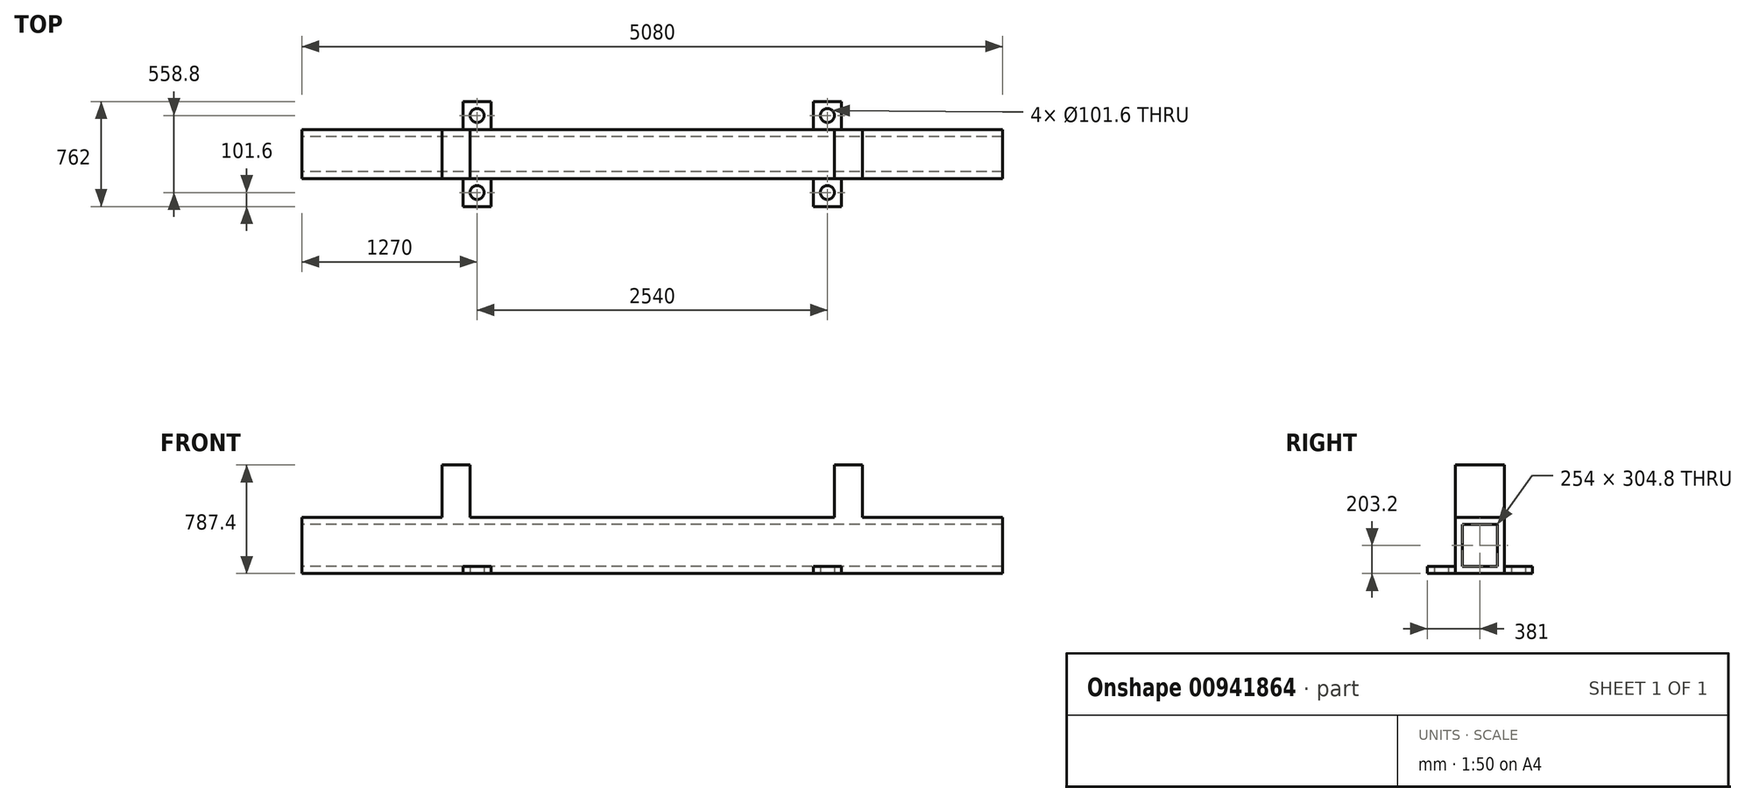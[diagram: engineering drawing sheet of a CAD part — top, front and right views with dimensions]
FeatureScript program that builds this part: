
annotation { "Feature Type Name" : "Feature", "Feature Type Description" : "" }
export const myFeature = defineFeature(function(context is Context, id is Id, definition is map)
    precondition{}
    {
        {
            var Q0;
            Q0=qCreatedBy(makeId("Top.planeOp"),FACE);
            var sketch = newSketch(context, id + "F0", { "sketchPlane" : qUnion([Q0])});
            skLineSegment(sketch, "E0.bottom", {"start": v(-2540, -177.8) * mm, "end": v(2540, -177.8) * mm});
            skLineSegment(sketch, "E0.top", {"start": v(-2540, 177.8) * mm, "end": v(2540, 177.8) * mm});
            skLineSegment(sketch, "E0.left", {"start": v(-2540, -177.8) * mm, "end": v(-2540, 177.8) * mm});
            skLineSegment(sketch, "E0.right", {"start": v(2540, -177.8) * mm, "end": v(2540, 177.8) * mm});
            skPoint(sketch, "E0.middle", {"position": v(0, 0) * mm});
            skLineSegment(sketch, "E1.bottom", {"start": v(-1371.6, -381) * mm, "end": v(-1168.4, -381) * mm});
            skLineSegment(sketch, "E1.top", {"start": v(-1371.6, 381) * mm, "end": v(-1168.4, 381) * mm});
            skLineSegment(sketch, "E1.left", {"start": v(-1371.6, -381) * mm, "end": v(-1371.6, 381) * mm});
            skLineSegment(sketch, "E1.right", {"start": v(-1168.4, -381) * mm, "end": v(-1168.4, 381) * mm});
            skPoint(sketch, "E1.middle", {"position": v(-1270, 0) * mm});
            skLineSegment(sketch, "E2.bottom", {"start": v(1168.4, -381) * mm, "end": v(1371.6, -381) * mm});
            skLineSegment(sketch, "E2.top", {"start": v(1168.4, 381) * mm, "end": v(1371.6, 381) * mm});
            skLineSegment(sketch, "E2.left", {"start": v(1168.4, -381) * mm, "end": v(1168.4, 381) * mm});
            skLineSegment(sketch, "E2.right", {"start": v(1371.6, -381) * mm, "end": v(1371.6, 381) * mm});
            skPoint(sketch, "E2.middle", {"position": v(1270, 0) * mm});
            skCircle(sketch, "E3", {"center": v(-1270, 279.4) * mm, "radius": 50.8 * mm});
            skCircle(sketch, "E4", {"center": v(-1270, -279.4) * mm, "radius": 50.8 * mm});
            skCircle(sketch, "E5", {"center": v(1270, 279.4) * mm, "radius": 50.8 * mm});
            skCircle(sketch, "E6", {"center": v(1270, -279.4) * mm, "radius": 50.8 * mm});
            skSolve(sketch);
        }
        {
            var Q0;
            {var subQ1=sQuery(id+"F0.wireOp",EDGE,"E1.top");Q0=makeQuery(id+"F0.imprint","IMPRINT",FACE,{"disambiguationData":[TD([[makeQuery(id+"F0.imprint","IMPRINT",EDGE,{"derivedFrom":subQ1}),-1.0]])]});}
            var Q1;
            {var subQ1=sQuery(id+"F0.wireOp",EDGE,"E1.bottom");Q1=makeQuery(id+"F0.imprint","IMPRINT",FACE,{"disambiguationData":[TD([[makeQuery(id+"F0.imprint","IMPRINT",EDGE,{"derivedFrom":subQ1}),1.0]])]});}
            var Q2;
            {var subQ0=sQuery(id+"F0.wireOp",EDGE,"E1.left");var subQ1=sQuery(id+"F0.wireOp",EDGE,"E0.bottom");var subQ2=makeQuery(id+"F0.imprint","INTERSECT",VERTEX,{"derivedFrom":[subQ1,subQ0]});Q2=makeQuery(id+"F0.imprint","IMPRINT",FACE,{"disambiguationData":[TD([[makeQuery(id+"F0.imprint","IMPRINT",EDGE,{"disambiguationData":[TD([[subQ2,-1.0]])],"derivedFrom":subQ1}),1.0]])]});}
            var Q3;
            {var subQ0=sQuery(id+"F0.wireOp",EDGE,"E1.right");var subQ1=sQuery(id+"F0.wireOp",EDGE,"E0.bottom");var subQ2=makeQuery(id+"F0.imprint","INTERSECT",VERTEX,{"derivedFrom":[subQ1,subQ0]});Q3=makeQuery(id+"F0.imprint","IMPRINT",FACE,{"disambiguationData":[TD([[makeQuery(id+"F0.imprint","IMPRINT",EDGE,{"disambiguationData":[TD([[subQ2,-1.0]])],"derivedFrom":subQ1}),1.0]])]});}
            var Q4;
            {var subQ0=sQuery(id+"F0.wireOp",EDGE,"E0.left");Q4=makeQuery(id+"F0.imprint","IMPRINT",FACE,{"disambiguationData":[TD([[makeQuery(id+"F0.imprint","IMPRINT",EDGE,{"derivedFrom":subQ0}),-1.0]])]});}
            var Q5;
            {var subQ0=sQuery(id+"F0.wireOp",EDGE,"E0.right");Q5=makeQuery(id+"F0.imprint","IMPRINT",FACE,{"disambiguationData":[TD([[makeQuery(id+"F0.imprint","IMPRINT",EDGE,{"derivedFrom":subQ0}),1.0]])]});}
            var Q6;
            {var subQ0=sQuery(id+"F0.wireOp",EDGE,"E2.left");var subQ1=sQuery(id+"F0.wireOp",EDGE,"E0.bottom");var subQ2=makeQuery(id+"F0.imprint","INTERSECT",VERTEX,{"derivedFrom":[subQ1,subQ0]});Q6=makeQuery(id+"F0.imprint","IMPRINT",FACE,{"disambiguationData":[TD([[makeQuery(id+"F0.imprint","IMPRINT",EDGE,{"disambiguationData":[TD([[subQ2,-1.0]])],"derivedFrom":subQ1}),1.0]])]});}
            var Q7;
            {var subQ1=sQuery(id+"F0.wireOp",EDGE,"E2.top");Q7=makeQuery(id+"F0.imprint","IMPRINT",FACE,{"disambiguationData":[TD([[makeQuery(id+"F0.imprint","IMPRINT",EDGE,{"derivedFrom":subQ1}),-1.0]])]});}
            var Q8;
            {var subQ1=sQuery(id+"F0.wireOp",EDGE,"E2.bottom");Q8=makeQuery(id+"F0.imprint","IMPRINT",FACE,{"disambiguationData":[TD([[makeQuery(id+"F0.imprint","IMPRINT",EDGE,{"derivedFrom":subQ1}),1.0]])]});}
            extrude(context, id + "F1", {"entities" : qUnion([Q0, Q1, Q2, Q3, Q4, Q5, Q6, Q7, Q8]), "depth" : 50.8 * mm, "offsetDistance" : 25.4 * mm});
        }
        {
            var Q0;
            {var subQ0=sQuery(id+"F0.wireOp",EDGE,"E1.right");var subQ1=sQuery(id+"F0.wireOp",EDGE,"E0.bottom");var subQ2=makeQuery(id+"F0.imprint","INTERSECT",VERTEX,{"derivedFrom":[subQ1,subQ0]});Q0=makeQuery(id+"F0.imprint","IMPRINT",FACE,{"disambiguationData":[TD([[makeQuery(id+"F0.imprint","IMPRINT",EDGE,{"disambiguationData":[TD([[subQ2,-1.0]])],"derivedFrom":subQ1}),1.0]])]});}
            var Q1;
            {var subQ0=sQuery(id+"F0.wireOp",EDGE,"E0.right");Q1=makeQuery(id+"F0.imprint","IMPRINT",FACE,{"disambiguationData":[TD([[makeQuery(id+"F0.imprint","IMPRINT",EDGE,{"derivedFrom":subQ0}),1.0]])]});}
            var Q2;
            {var subQ0=sQuery(id+"F0.wireOp",EDGE,"E0.left");Q2=makeQuery(id+"F0.imprint","IMPRINT",FACE,{"disambiguationData":[TD([[makeQuery(id+"F0.imprint","IMPRINT",EDGE,{"derivedFrom":subQ0}),-1.0]])]});}
            var Q3;
            {var subQ0=sQuery(id+"F0.wireOp",EDGE,"E1.left");var subQ1=sQuery(id+"F0.wireOp",EDGE,"E0.bottom");var subQ2=makeQuery(id+"F0.imprint","INTERSECT",VERTEX,{"derivedFrom":[subQ1,subQ0]});Q3=makeQuery(id+"F0.imprint","IMPRINT",FACE,{"disambiguationData":[TD([[makeQuery(id+"F0.imprint","IMPRINT",EDGE,{"disambiguationData":[TD([[subQ2,-1.0]])],"derivedFrom":subQ1}),1.0]])]});}
            var Q4;
            {var subQ0=sQuery(id+"F0.wireOp",EDGE,"E2.left");var subQ1=sQuery(id+"F0.wireOp",EDGE,"E0.bottom");var subQ2=makeQuery(id+"F0.imprint","INTERSECT",VERTEX,{"derivedFrom":[subQ1,subQ0]});Q4=makeQuery(id+"F0.imprint","IMPRINT",FACE,{"disambiguationData":[TD([[makeQuery(id+"F0.imprint","IMPRINT",EDGE,{"disambiguationData":[TD([[subQ2,-1.0]])],"derivedFrom":subQ1}),1.0]])]});}
            extrude(context, id + "F2", {"entities" : qUnion([Q0, Q1, Q2, Q3, Q4]), "operationType" : NewBodyOperationType.ADD, "depth" : 406.4 * mm, "offsetDistance" : 25.4 * mm});
        }
        {
            var Q0;
            {var subQ0=sQuery(id+"F0.wireOp",EDGE,"E0.left");Q0=makeQuery(id+"F2.boolean.opBoolean","MERGE",FACE,{"derivedFrom":[makeQuery(id+"F1.opExtrude","SWEPT_FACE",FACE,{"disambiguationData":[OSD([subQ0])]}),makeQuery(id+"F2.opExtrude","SWEPT_FACE",FACE,{"disambiguationData":[OSD([subQ0])]})]});}
            var sketch = newSketch(context, id + "F3", { "sketchPlane" : qUnion([Q0])});
            skLineSegment(sketch, "E7.bottom", {"start": v(-127, 50.8) * mm, "end": v(127, 50.8) * mm});
            skLineSegment(sketch, "E7.top", {"start": v(-127, 355.6) * mm, "end": v(127, 355.6) * mm});
            skLineSegment(sketch, "E7.left", {"start": v(-127, 50.8) * mm, "end": v(-127, 355.6) * mm});
            skLineSegment(sketch, "E7.right", {"start": v(127, 50.8) * mm, "end": v(127, 355.6) * mm});
            skPoint(sketch, "E7.middle", {"position": v(0, 203.2) * mm});
            skLineSegment(sketch, "E8.bottom", {"start": v(127, 355.6) * mm, "end": v(228.6, 355.6) * mm});
            skLineSegment(sketch, "E8.top", {"start": v(127, 203.2) * mm, "end": v(228.6, 203.2) * mm});
            skLineSegment(sketch, "E8.left", {"start": v(127, 355.6) * mm, "end": v(127, 203.2) * mm});
            skLineSegment(sketch, "E8.right", {"start": v(228.6, 355.6) * mm, "end": v(228.6, 203.2) * mm});
            skSolve(sketch);
        }
        {
            var Q0;
            Q0=makeQuery(id+"F3.imprint","IMPRINT",FACE,{"disambiguationData":[TD([[makeQuery(id+"F3.imprint","IMPRINT",EDGE,{"derivedFrom":sQuery(id+"F3.wireOp",EDGE,"E7.bottom")}),1.0]])]});
            var Q1;
            {var subQ0=sQuery(id+"F3.wireOp",EDGE,"E8.right");Q1=makeQuery(id+"F3.imprint","IMPRINT",FACE,{"disambiguationData":[TD([[makeQuery(id+"F3.imprint","IMPRINT",EDGE,{"derivedFrom":subQ0}),-1.0]])]});}
            var Q2;
            {var subQ0=sQuery(id+"F3.wireOp",EDGE,"E8.left");Q2=makeQuery(id+"F3.imprint","IMPRINT",FACE,{"disambiguationData":[TD([[makeQuery(id+"F3.imprint","IMPRINT",EDGE,{"derivedFrom":subQ0}),1.0]])]});}
            extrude(context, id + "F4", {"entities" : qUnion([Q0, Q1, Q2]), "operationType" : NewBodyOperationType.REMOVE, "oppositeDirection" : true, "depth" : 5963.92 * mm, "offsetDistance" : 25.4 * mm});
        }
        {
            var Q0;
            Q0=makeQuery(id+"F2.opExtrude","CAP_FACE",FACE,{"disambiguationData":[OSD([sQuery(id+"F0.wireOp",EDGE,"E0.bottom"),sQuery(id+"F0.wireOp",EDGE,"E0.top"),sQuery(id+"F0.wireOp",EDGE,"E0.left"),sQuery(id+"F0.wireOp",EDGE,"E0.right")])],"isStart":false});
            var sketch = newSketch(context, id + "F5", { "sketchPlane" : qUnion([Q0])});
            skPoint(sketch, "E9.middle", {"position": v(-1422.4, 0) * mm});
            skLineSegment(sketch, "E10", {"start": v(0, 0) * mm, "end": v(-2540, 0) * mm});
            skLineSegment(sketch, "E11", {"start": v(0, 0) * mm, "end": v(2540, 0) * mm});
            skPoint(sketch, "E12", {"position": v(1422.4, 0) * mm});
            skLineSegment(sketch, "E13.bottom", {"start": v(1320.8, -177.8) * mm, "end": v(1524, -177.8) * mm});
            skLineSegment(sketch, "E13.top", {"start": v(1320.8, 177.8) * mm, "end": v(1524, 177.8) * mm});
            skLineSegment(sketch, "E13.left", {"start": v(1320.8, -177.8) * mm, "end": v(1320.8, 177.8) * mm});
            skLineSegment(sketch, "E13.right", {"start": v(1524, -177.8) * mm, "end": v(1524, 177.8) * mm});
            skLineSegment(sketch, "E14.bottom", {"start": v(-1320.8, 177.8) * mm, "end": v(-1524, 177.8) * mm});
            skLineSegment(sketch, "E14.top", {"start": v(-1320.8, -177.8) * mm, "end": v(-1524, -177.8) * mm});
            skLineSegment(sketch, "E14.left", {"start": v(-1320.8, 177.8) * mm, "end": v(-1320.8, -177.8) * mm});
            skLineSegment(sketch, "E14.right", {"start": v(-1524, 177.8) * mm, "end": v(-1524, -177.8) * mm});
            skSolve(sketch);
        }
        {
            var Q0;
            {var subQ5=sQuery(id+"F5.wireOp",EDGE,"E13.top");Q0=makeQuery(id+"F5.imprint","IMPRINT",FACE,{"disambiguationData":[TD([[makeQuery(id+"F5.imprint","IMPRINT",EDGE,{"derivedFrom":subQ5}),-1.0]])]});}
            var Q1;
            {var subQ5=sQuery(id+"F5.wireOp",EDGE,"E13.bottom");Q1=makeQuery(id+"F5.imprint","IMPRINT",FACE,{"disambiguationData":[TD([[makeQuery(id+"F5.imprint","IMPRINT",EDGE,{"derivedFrom":subQ5}),1.0]])]});}
            var Q2;
            {var subQ5=sQuery(id+"F5.wireOp",EDGE,"E14.top");Q2=makeQuery(id+"F5.imprint","IMPRINT",FACE,{"disambiguationData":[TD([[makeQuery(id+"F5.imprint","IMPRINT",EDGE,{"derivedFrom":subQ5}),1.0]])]});}
            var Q3;
            {var subQ5=sQuery(id+"F5.wireOp",EDGE,"E14.bottom");Q3=makeQuery(id+"F5.imprint","IMPRINT",FACE,{"disambiguationData":[TD([[makeQuery(id+"F5.imprint","IMPRINT",EDGE,{"derivedFrom":subQ5}),-1.0]])]});}
            extrude(context, id + "F6", {"entities" : qUnion([Q0, Q1, Q2, Q3]), "operationType" : NewBodyOperationType.ADD, "depth" : 381 * mm, "offsetDistance" : 25.4 * mm});
        }
    });
